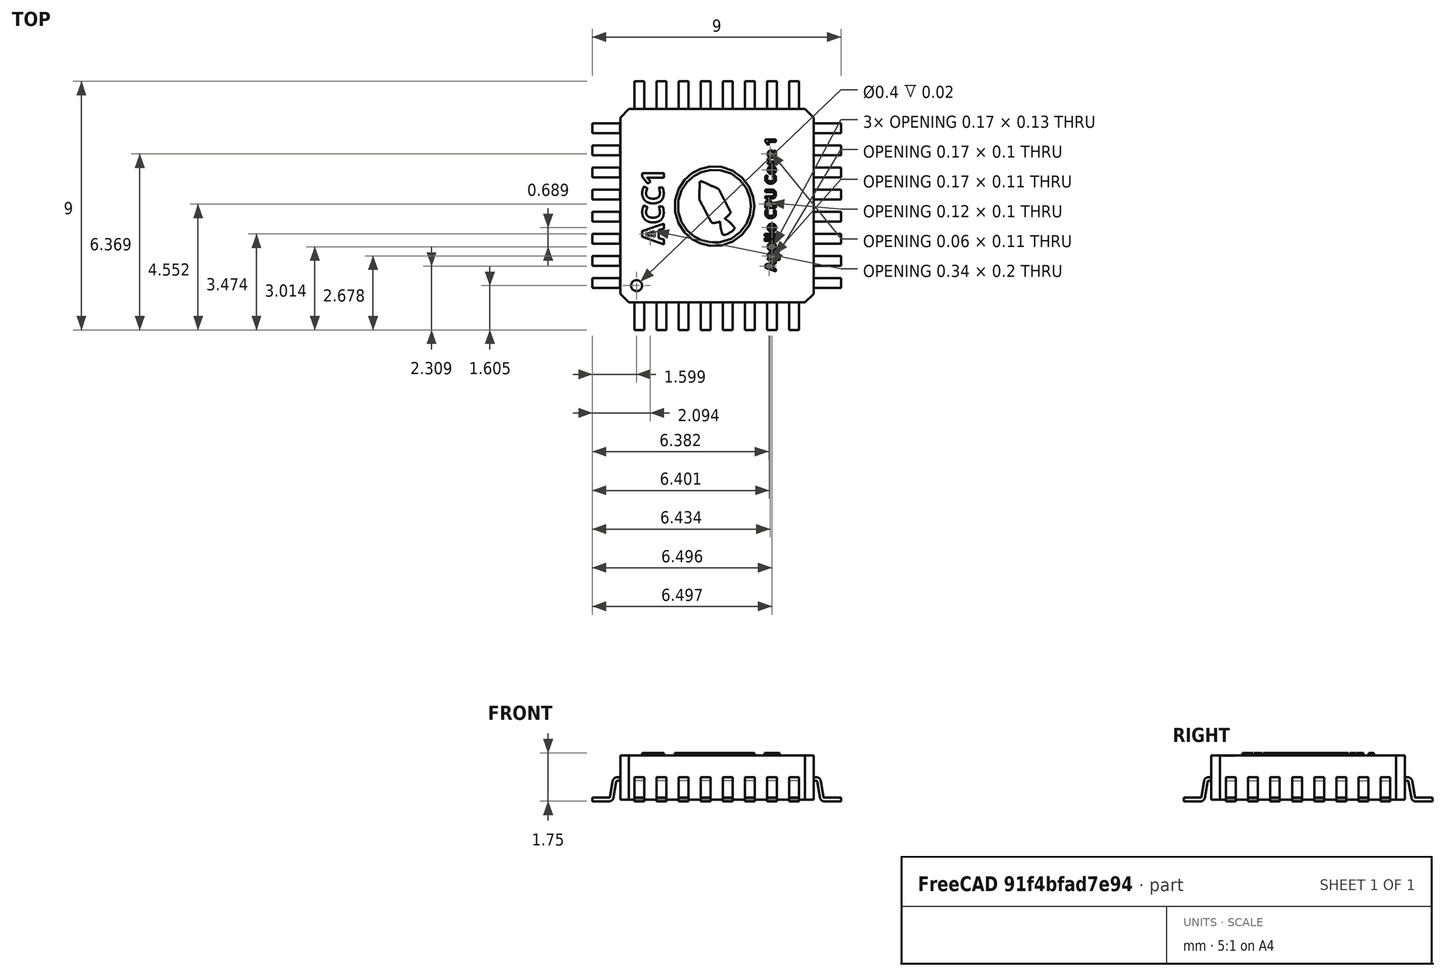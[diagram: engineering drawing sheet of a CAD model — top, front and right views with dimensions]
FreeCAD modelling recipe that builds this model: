
FCSTD DOCUMENT  (FreeCAD 0.16R6703 (Git))
Label: ACC1-chip
License: CC-BY 3.0
LicenseURL: http://creativecommons.org/licenses/by/3.0/
objects: Part::Extrusion×5, Part::Part2DObjectPython×4, Part::FeaturePython×2, Part::Compound×1, Part::Cut×1, Part::MultiFuse×1, App::DocumentObjectGroup×1
note: 14 computed .brp shape members not serialized (recipe doc carries the construction recipe); baked Part::Feature solids carry a one-line shape summary decoded from their .brp

FEATURE [Part::Part2DObjectPython] ShapeString  # Draft 2D object (typed FeaturePython)
  FontFile = <userpath>/develop/fpgawars.github.io/images/src/Open_Sans/OpenSans-Bold.ttf
  Placement = pos=(-9.34532,3.35513,3.3) rot=(0,0,1;0rad)
  Size = 1
  String = ACC1
  Tracking = 0
FEATURE [Part::Extrusion] Extrude001  label="ACC-text"
  Base = -> ShapeString
  Dir = (0,0,0.1)
  Placement = pos=(0.248823,3.2993,0) rot=(0,0,1;1.5708rad)
  Solid = true
FEATURE [Part::Part2DObjectPython] ShapeString001  # Draft 2D object (typed FeaturePython)
  FontFile = <userpath>/develop/fpgawars.github.io/images/src/Open_Sans/OpenSans-Bold.ttf
  Placement = pos=(-9.34532,3.35513,3.3) rot=(0,0,1;0rad)
  Size = 0.5
  String = Apollo CPU Core 1
  Tracking = 0
FEATURE [Part::Extrusion] Extrude002  label="Apollo-cpu-core-Text"
  Base = -> ShapeString001
  Dir = (0,0,0.1)
  Placement = pos=(4.31116,2.32437,0) rot=(0,0,1;1.5708rad)
  Solid = true
FEATURE [Part::Compound] Compound021  label="PQFP-035"
  Placement = pos=(-5.71099,-9.13488,1.7) rot=(0,0,1;0rad)
FEATURE [Part::Extrusion] Extrude  label="logo-orig"
  Dir = (0,0,0.1)
  Placement = pos=(0,0,0) rot=(0,0,1;1.5708rad)
  Solid = true
FEATURE [Part::FeaturePython] Clone  label="logo-ship"  # Draft clone (typed FeaturePython)
  Objects = -> [Extrude]
  Placement = pos=(0.0455738,-4.76068,3.3) rot=(0,0,1;1.5708rad)
  Scale = (0.03,0.03,1)
FEATURE [Part::Part2DObjectPython] Circle  # Draft 2D object (typed FeaturePython)
  FirstAngle = 0
  LastAngle = 0
  MakeFace = true
  Placement = pos=(-0.174267,-5.64836,3.3) rot=(0,0,1;0rad)
  Radius = 1.65
FEATURE [Part::Extrusion] Extrude003  label="Inner-ring"
  Base = -> Circle
  Dir = (0,0,0.3)
  Placement = pos=(0,0,-0.1) rot=(0,0,1;0rad)
  Solid = true
FEATURE [Part::Part2DObjectPython] Circle001  # Draft 2D object (typed FeaturePython)
  FirstAngle = 0
  LastAngle = 0
  MakeFace = true
  Placement = pos=(-0.174267,-5.64836,3.3) rot=(0,0,1;0rad)
  Radius = 1.8
FEATURE [Part::Extrusion] Extrude004  label="Exterior-ring"
  Base = -> Circle001
  Dir = (0,0,0.1)
  Solid = true
FEATURE [Part::Cut] Cut  label="ring"
  Base = -> Extrude004
  Placement = pos=(0.0722774,0.922711,0) rot=(0,0,1;0rad)
  Tool = -> Extrude003
FEATURE [Part::MultiFuse] Fusion  label="logo-union"
  Placement = pos=(-1.14314,0.0422994,0) rot=(0,0,1;0rad)
  Shapes = -> [Clone,Cut]
FEATURE [Part::FeaturePython] Clone001  label="logo"  # Draft clone (typed FeaturePython)
  Objects = -> [Fusion]
  Placement = pos=(-1.4157,-0.869748,0) rot=(0,0,1;0rad)
  Scale = (0.8,0.8,1)
FEATURE [App::DocumentObjectGroup] Group  label="logo-src"
  Group = -> [Extrude,Fusion]
